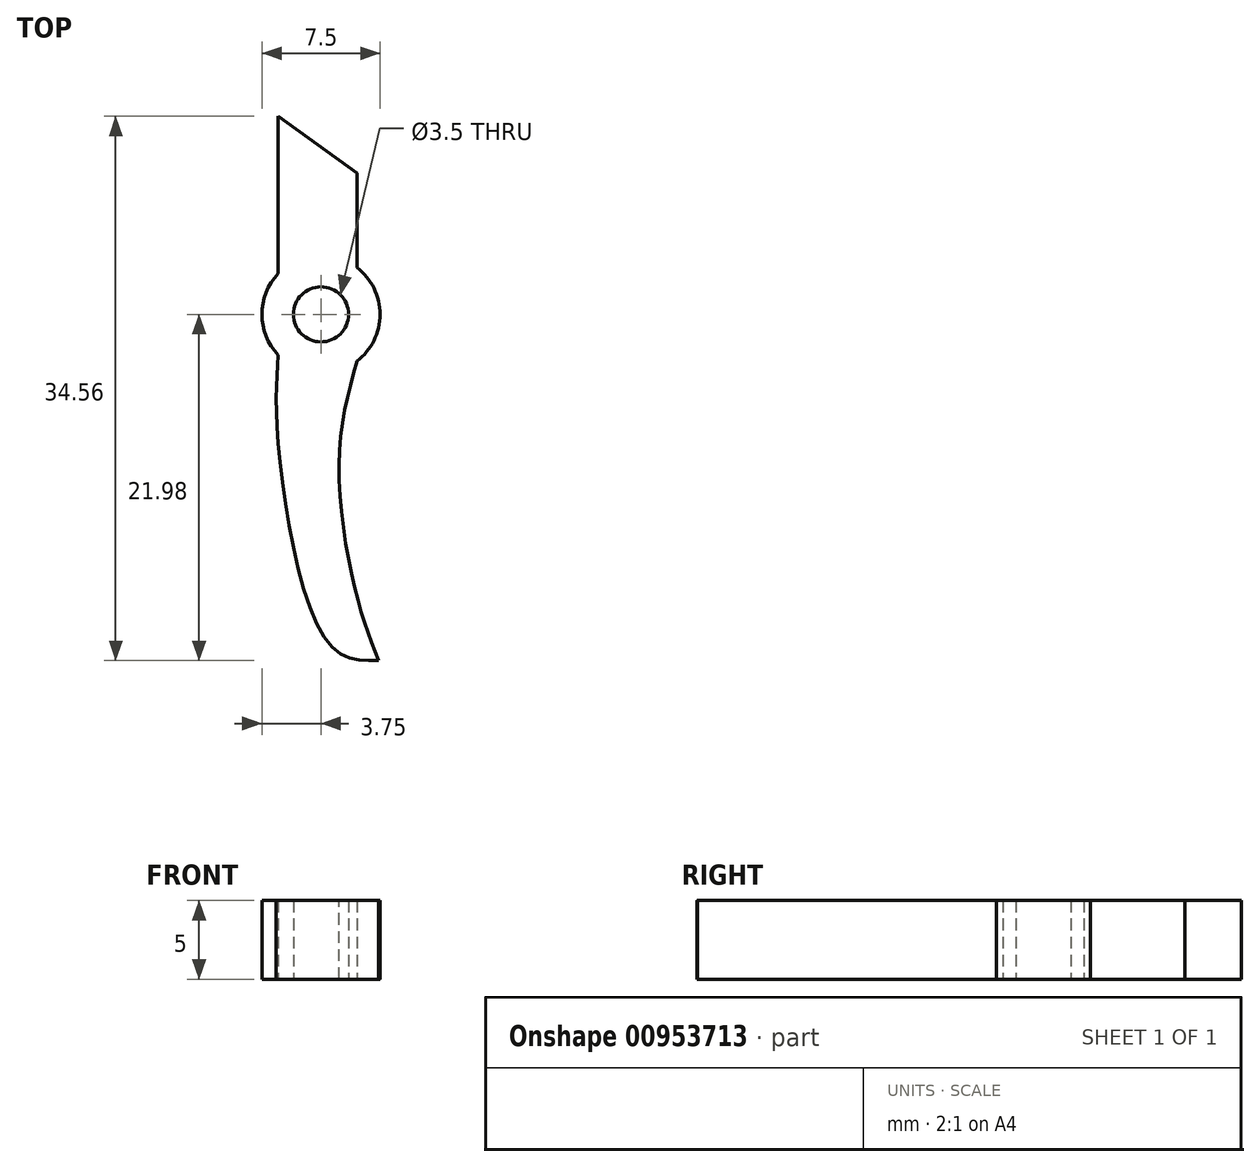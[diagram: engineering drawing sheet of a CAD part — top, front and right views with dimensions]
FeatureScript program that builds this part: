
annotation { "Feature Type Name" : "Feature", "Feature Type Description" : "" }
export const myFeature = defineFeature(function(context is Context, id is Id, definition is map)
    precondition{}
    {
        {
            var Q0;
            Q0=qCreatedBy(makeId("Top.planeOp"),FACE);
            var sketch = newSketch(context, id + "F0", { "sketchPlane" : qUnion([Q0])});
            skCircle(sketch, "E0", {"center": v(0, 0) * mm, "radius": 1.75 * mm});
            skCircle(sketch, "E1", {"center": v(0, 0) * mm, "radius": 3.75 * mm});
            skLineSegment(sketch, "E2", {"start": v(-2.72, 2.58) * mm, "end": v(-2.72, 12.58) * mm});
            skLineSegment(sketch, "E3", {"start": v(-2.72, 12.58) * mm, "end": v(2.28, 8.98) * mm});
            skLineSegment(sketch, "E4", {"start": v(2.28, 8.98) * mm, "end": v(2.28, 2.98) * mm});
            skFitSpline(sketch, "E5", {"points": [v(-2.72, -2.58) * mm, v(-2.72, -8.12) * mm, v(0.53, -20.94) * mm, v(3.64, -21.98) * mm], "startDerivative": vector(-1.05, -14.7) * mm, "endDerivative": vector(14.22, 0.3) * mm});
            skFitSpline(sketch, "E6", {"points": [v(2.28, -2.98) * mm, v(1.15, -9.3) * mm, v(2.28, -17.9) * mm, v(3.64, -21.98) * mm], "startDerivative": vector(-4.8, -17.52) * mm, "endDerivative": vector(5.04, -13.07) * mm});
            skSolve(sketch);
        }
        {
            var Q0;
            Q0 = qSketchRegion(id + "F0", true);
            extrude(context, id + "F1", {"entities" : qUnion([Q0]), "depth" : 5 * mm, "offsetDistance" : 25 * mm});
        }
    });
